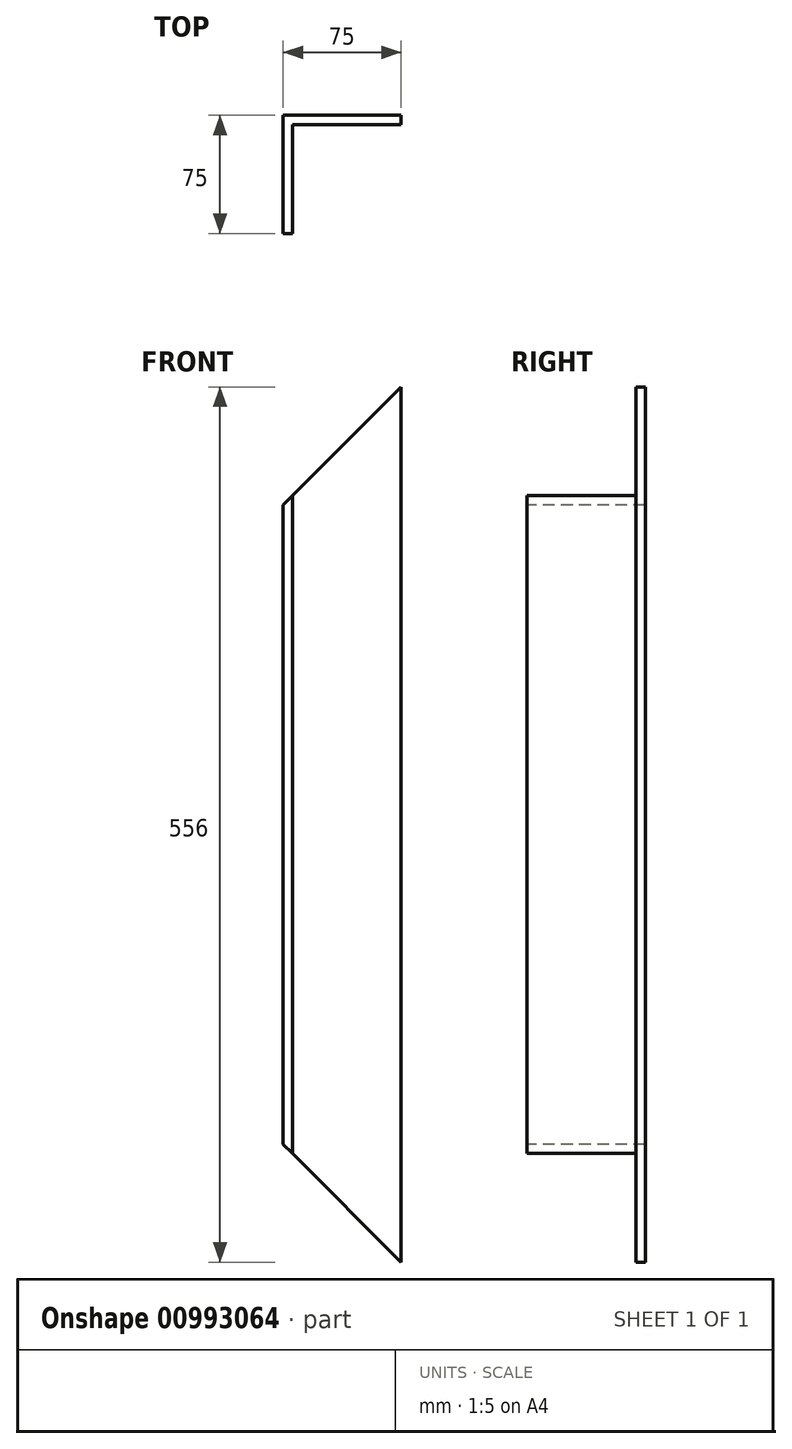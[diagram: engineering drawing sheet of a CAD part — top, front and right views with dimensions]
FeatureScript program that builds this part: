
annotation { "Feature Type Name" : "Feature", "Feature Type Description" : "" }
export const myFeature = defineFeature(function(context is Context, id is Id, definition is map)
    precondition{}
    {
        {
            var Q0;
            Q0=qCreatedBy(makeId("Top.planeOp"),FACE);
            var sketch = newSketch(context, id + "F0", { "sketchPlane" : qUnion([Q0])});
            skLineSegment(sketch, "E0", {"start": v(0, 0) * mm, "end": v(0, 75) * mm});
            skLineSegment(sketch, "E1", {"start": v(0, 75) * mm, "end": v(6, 75) * mm});
            skLineSegment(sketch, "E2", {"start": v(6, 75) * mm, "end": v(6, 6) * mm});
            skLineSegment(sketch, "E3", {"start": v(6, 6) * mm, "end": v(75, 6) * mm});
            skLineSegment(sketch, "E4", {"start": v(75, 6) * mm, "end": v(75, 0) * mm});
            skLineSegment(sketch, "E5", {"start": v(75, 0) * mm, "end": v(0, 0) * mm});
            skSolve(sketch);
        }
        {
            var Q0;
            Q0=makeQuery(id+"F0.imprint","IMPRINT",FACE,{"disambiguationData":[TD([[makeQuery(id+"F0.imprint","IMPRINT",EDGE,{"derivedFrom":sQuery(id+"F0.wireOp",EDGE,"E0")}),-1.0]])]});
            extrude(context, id + "F1", {"entities" : qUnion([Q0]), "depth" : 556 * mm, "offsetDistance" : 25 * mm});
        }
        {
            var Q0;
            Q0=qCreatedBy(makeId("Front.planeOp"),FACE);
            var sketch = newSketch(context, id + "F2", { "sketchPlane" : qUnion([Q0])});
            skLineSegment(sketch, "E6", {"start": v(0, 0) * mm, "end": v(75, 0) * mm});
            skLineSegment(sketch, "E7", {"start": v(75, 0) * mm, "end": v(0, 75) * mm});
            skLineSegment(sketch, "E8", {"start": v(0, 75) * mm, "end": v(0, 0) * mm});
            skSolve(sketch);
        }
        {
            var Q0;
            Q0=makeQuery(id+"F2.imprint","IMPRINT",FACE,{"disambiguationData":[TD([[makeQuery(id+"F2.imprint","IMPRINT",EDGE,{"derivedFrom":sQuery(id+"F2.wireOp",EDGE,"E6")}),1.0]])]});
            extrude(context, id + "F3", {"entities" : qUnion([Q0]), "operationType" : NewBodyOperationType.REMOVE, "endBound" : BoundingType.THROUGH_ALL, "oppositeDirection" : true, "depth" : 25 * mm, "offsetDistance" : 25 * mm});
        }
        {
            var Q0;
            Q0=qCreatedBy(makeId("Front.planeOp"),FACE);
            var sketch = newSketch(context, id + "F4", { "sketchPlane" : qUnion([Q0])});
            skLineSegment(sketch, "E9", {"start": v(75, 556) * mm, "end": v(0, 481) * mm});
            skLineSegment(sketch, "E10", {"start": v(0, 481) * mm, "end": v(0, 556) * mm});
            skLineSegment(sketch, "E11", {"start": v(0, 556) * mm, "end": v(75, 556) * mm});
            skSolve(sketch);
        }
        {
            var Q0;
            Q0=makeQuery(id+"F4.imprint","IMPRINT",FACE,{"disambiguationData":[TD([[makeQuery(id+"F4.imprint","IMPRINT",EDGE,{"derivedFrom":sQuery(id+"F4.wireOp",EDGE,"E9")}),-1.0]])]});
            extrude(context, id + "F5", {"entities" : qUnion([Q0]), "operationType" : NewBodyOperationType.REMOVE, "endBound" : BoundingType.THROUGH_ALL, "oppositeDirection" : true, "depth" : 25 * mm, "offsetDistance" : 25 * mm});
        }
        {
            var Q0;
            Q0=makeQuery(id+"F1.opExtrude","SWEPT_BODY",BODY,{"disambiguationData":[OSD([sQuery(id+"F0.wireOp",EDGE,"E0"),sQuery(id+"F0.wireOp",EDGE,"E1"),sQuery(id+"F0.wireOp",EDGE,"E2"),sQuery(id+"F0.wireOp",EDGE,"E3"),sQuery(id+"F0.wireOp",EDGE,"E4"),sQuery(id+"F0.wireOp",EDGE,"E5")])]});
            var Q1;
            Q1=qCreatedBy(makeId("Front.planeOp"),FACE);
            mirror(context, id + "F6", {"operationType" : NewBodyOperationType.ADD, "entities" : qUnion([Q0]), "mirrorPlane" : qUnion([Q1])});
        }
        {
            var Q0;
            Q0=qCreatedBy(makeId("Top.planeOp"),FACE);
            var sketch = newSketch(context, id + "F7", { "sketchPlane" : qUnion([Q0])});
            skLineSegment(sketch, "E12", {"start": v(0, 0) * mm, "end": v(75, 0) * mm});
            skLineSegment(sketch, "E13", {"start": v(75, 0) * mm, "end": v(75, 75) * mm});
            skLineSegment(sketch, "E14", {"start": v(75, 75) * mm, "end": v(0, 75) * mm});
            skLineSegment(sketch, "E15", {"start": v(0, 75) * mm, "end": v(0, 0) * mm});
            skLineSegment(sketch, "E16", {"start": v(0, 0) * mm, "end": v(0, 0) * mm});
            skSolve(sketch);
        }
        {
            var Q0;
            Q0=makeQuery(id+"F7.imprint","IMPRINT",FACE,{"disambiguationData":[TD([[makeQuery(id+"F7.imprint","IMPRINT",EDGE,{"derivedFrom":sQuery(id+"F7.wireOp",EDGE,"E12")}),1.0]])]});
            extrude(context, id + "F8", {"entities" : qUnion([Q0]), "operationType" : NewBodyOperationType.REMOVE, "endBound" : BoundingType.THROUGH_ALL, "depth" : 25 * mm, "offsetDistance" : 25 * mm});
        }
    });
